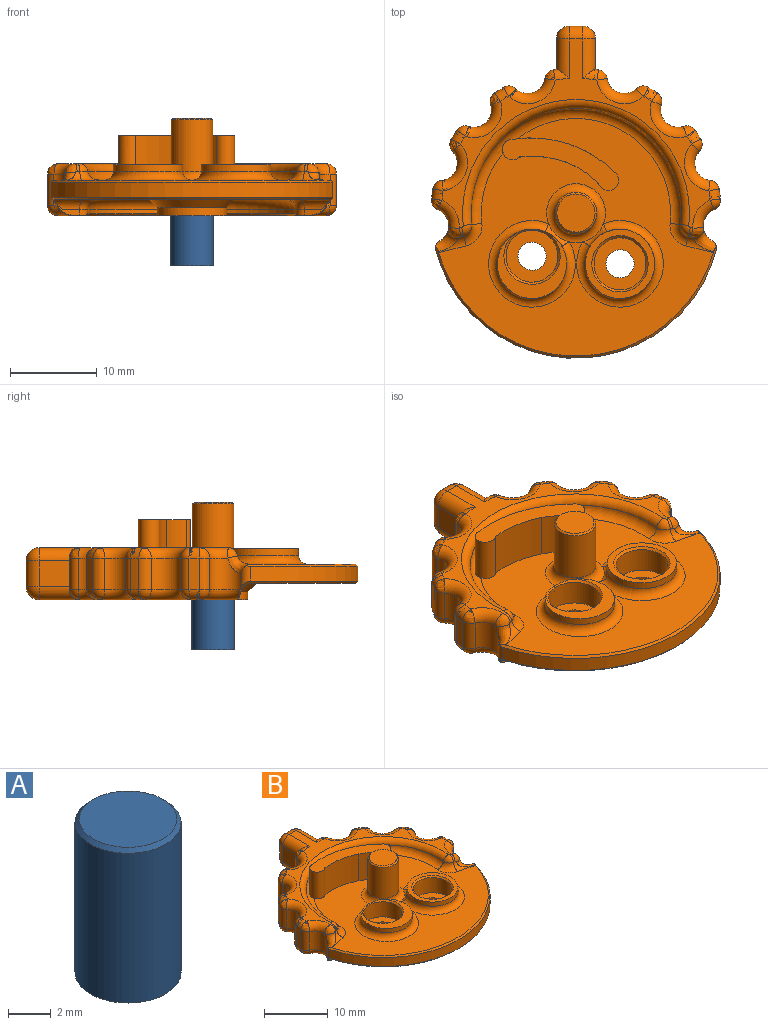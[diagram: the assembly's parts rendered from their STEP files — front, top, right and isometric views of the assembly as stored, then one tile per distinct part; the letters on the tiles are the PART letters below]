
ASSEMBLY  parts=2 mates=1
PART A: 4 faces, bbox 5x5x8.8 mm
  f0: cylinder r=2.48mm len=8.55mm, axis (0,0,-1), area 133mm2, adj f2,f3
  f1: plane 4.55x4.55mm, normal (0,0,1), area 16.3mm2, adj f3
  f2: plane 4.95x4.95mm, normal (0,0,-1), area 19.2mm2, adj f0
  f3: cone r=2.27mm half-angle=45deg, axis (0,0,-1), area 4.2mm2, adj f0,f1
PART B: 180 faces, bbox 33.4x38.4x11.5 mm
  f0: plane 31.71x27.42mm, normal (0,0,-1), area 478mm2, adj f1,f168,f169,f170,f171,f172,f173,f174
  f1: cylinder r=1.2mm len=3.47mm, axis (-0.97,0.24,0), area 5.1mm2, adj f0,f2,f168,f172
  f2: plane 2.59x1.21mm, normal (-0.24,-0.97,0), area 1.2mm2, adj f1,f3,f166,f167,f172
  f3: bspline ~1.85x1.33mm, area 0.3mm2, adj f2,f4,f165,f166
  f4: torus R=3.2mm, axis (0,0,1), area 8.5mm2, adj f3,f5,f163,f164
  f5: sphere r=1.2mm, area 1.8mm2, adj f4,f6,f162
  f6: cylinder r=1.2mm len=3.6mm, axis (0,0,1), area 5.5mm2, adj f5,f7,f161,f164
  f7: cylinder r=16.75mm len=3.6mm, axis (0,0,-1), area 4.3mm2, adj f6,f8,f160,f162
  f8: torus R=15.55mm, axis (0,0,1), area 2.2mm2, adj f7,f9,f159,f161
  f9: plane 30.96x21.83mm, normal (0,0,1), area 67mm2, adj f8,f10,f137,f138,f139,f140,f141,f142
  f10: cylinder r=1.5mm len=1.5mm, axis (1,0,0), area 3.5mm2, adj f9,f11,f135,f136
  f11: plane 3x1.5mm, normal (0,1,0), area 4.5mm2, adj f10,f12,f101,f134
  f12: cylinder r=1.5mm len=3mm, axis (0,0,1), area 7.1mm2, adj f11,f13,f100,f136
  f13: plane 3.5x3mm, normal (-1,0,0), area 10.5mm2, adj f12,f14,f99,f158
  f14: cylinder r=16.75mm len=3.6mm, axis (0,0,-1), area 1.3mm2, adj f13,f15,f98,f99,f157,f158
  f15: cylinder r=1.2mm len=3.6mm, axis (0,0,1), area 5.5mm2, adj f14,f16,f96,f97
  f16: cylinder r=2mm len=3.6mm, axis (0,0,-1), area 15.7mm2, adj f15,f17,f94,f156
  f17: torus R=3.2mm, axis (0,0,1), area 10mm2, adj f16,f18,f96,f163
  f18: sphere r=1.2mm, area 1mm2, adj f17,f19,f94
  f19: torus R=15.55mm, axis (0,0,1), area 2.2mm2, adj f18,f20,f93,f163
  f20: cylinder r=16.75mm len=3.6mm, axis (0,0,-1), area 4.3mm2, adj f19,f21,f94,f155
  f21: cylinder r=1.2mm len=3.6mm, axis (0,0,1), area 5.5mm2, adj f20,f22,f23,f93
  f22: sphere r=1.2mm, area 1mm2, adj f21,f154,f155
  f23: cylinder r=2mm len=3.6mm, axis (0,0,-1), area 15.8mm2, adj f21,f24,f91,f154
  f24: torus R=3.2mm, axis (0,0,1), area 10.1mm2, adj f23,f25,f93,f163
  f25: sphere r=1.2mm, area 1mm2, adj f24,f26,f91
  f26: torus R=15.55mm, axis (0,0,1), area 2.2mm2, adj f25,f27,f90,f163
  f27: cylinder r=16.75mm len=3.6mm, axis (0,0,-1), area 4.3mm2, adj f26,f28,f91,f153
  f28: cylinder r=1.2mm len=3.6mm, axis (0,0,1), area 5.6mm2, adj f27,f29,f30,f90
  f29: sphere r=1.2mm, area 1mm2, adj f28,f152,f153
  f30: cylinder r=2mm len=3.6mm, axis (0,0,-1), area 15.9mm2, adj f28,f31,f88,f152
  f31: torus R=3.2mm, axis (0,0,1), area 10.1mm2, adj f30,f32,f90,f163
  f32: sphere r=1.2mm, area 1mm2, adj f31,f33,f88
  f33: torus R=15.55mm, axis (0,0,1), area 2.2mm2, adj f32,f34,f87,f163
  f34: cylinder r=16.75mm len=3.6mm, axis (0,0,-1), area 4.3mm2, adj f33,f35,f88,f151
  f35: cylinder r=1.2mm len=3.6mm, axis (0,0,1), area 5.5mm2, adj f34,f36,f37,f87
  f36: sphere r=1.2mm, area 1mm2, adj f35,f150,f151
  f37: cylinder r=2mm len=3.6mm, axis (0,0,-1), area 13.7mm2, adj f35,f38,f47,f48,f86,f150,f172
  f38: torus R=3.2mm, axis (0,0,1), area 8.5mm2, adj f37,f39,f87,f163
  f39: bspline ~1.85x1.33mm, area 0.3mm2, adj f38,f40,f46,f47
  f40: plane 2.59x1.21mm, normal (0.24,-0.97,0), area 1.2mm2, adj f39,f41,f46,f171,f172
  f41: cylinder r=1.2mm len=1.3mm, axis (0,0,-1), area 1mm2, adj f40,f42,f43,f45,f170
  f42: cylinder r=12.12mm len=24.25mm, axis (0,0,-1), area 18.3mm2, adj f41,f43,f167,f169
  f43: cone r=12.37mm half-angle=45deg, axis (0,0,-1), area 14.9mm2, adj f41,f42,f44,f45,f163,f167
  f44: cone r=1.13mm half-angle=45deg, axis (0,0,1), area 0.1mm2, adj f43,f163,f166,f167
  f45: cone r=1.13mm half-angle=45deg, axis (0,0,1), area 0.1mm2, adj f41,f43,f46,f163
  f46: plane 0.79x0.26mm, normal (0.17,-0.69,-0.71), area 0.1mm2, adj f39,f40,f45,f163
  f47: plane 0.13x0.06mm, normal (-0.91,-0.41,0), area 0mm2, adj f37,f39,f172
  f48: cylinder r=1mm len=2.52mm, axis (0,0,1), area 2.5mm2, adj f37,f49,f85,f86,f172
  f49: cone r=16.5mm half-angle=45deg, axis (0,0,-1), area 15.6mm2, adj f48,f50,f79,f81,f82,f83,f85,f86
  f50: plane 31.71x27.42mm, normal (0,0,1), area 353.1mm2, adj f49,f51,f53,f54,f55,f56,f57,f58
  f51: cylinder r=1.18mm len=5.15mm, axis (0,0,-1), area 24.1mm2, adj f50,f52,f53,f57,f58
  f52: plane 13.41x6.07mm, normal (0,0,1), area 30.4mm2, adj f51,f53,f54,f56,f57
  f53: cylinder r=11.53mm len=6.5mm, axis (0,0,-1), area 34.4mm2, adj f50,f51,f52,f54
  f54: cylinder r=9.21mm len=7.81mm, axis (0,0,-1), area 19.3mm2, adj f50,f52,f53,f55,f56,f175
  f55: cylinder r=1.18mm len=2.66mm, axis (0,0,-1), area 0.1mm2, adj f50,f54,f175
  f56: cylinder r=1.18mm len=5.15mm, axis (0,0,-1), area 19.7mm2, adj f50,f52,f54,f57
  f57: cylinder r=13.74mm len=11.77mm, axis (0,0,-1), area 66.2mm2, adj f50,f51,f52,f56,f58
  f58: torus R=10.92mm, axis (0,0,1), area 66.3mm2, adj f50,f51,f57,f59,f60,f147
  f59: torus R=2.4mm, axis (0,0,1), area 4.2mm2, adj f50,f58,f79,f146
  f60: torus R=2.4mm, axis (0,0,1), area 4.2mm2, adj f50,f58,f83,f148
  f61: torus R=5mm, axis (0,0,1), area 38.6mm2, adj f50,f62,f63
  f62: bspline ~2.78x2.59mm, area 3mm2, adj f61,f63,f75
  f63: cylinder r=4mm len=8mm, axis (0,0,-1), area 20.1mm2, adj f61,f62,f64
  f64: plane 8x8mm, normal (0,0,1), area 17.1mm2, adj f63,f65
  f65: cone r=3.25mm half-angle=45deg, axis (0,0,1), area 6.9mm2, adj f64,f66
  f66: cylinder r=3mm len=6mm, axis (0,0,-1), area 54.7mm2, adj f65,f67
  f67: plane 6x6mm, normal (0,0,1), area 20mm2, adj f66,f173
  f68: torus R=5mm, axis (0,0,1), area 38.6mm2, adj f50,f69,f70
  f69: bspline ~2.78x2.59mm, area 3mm2, adj f68,f70,f75
  f70: cylinder r=4mm len=8mm, axis (0,0,-1), area 20.1mm2, adj f68,f69,f71,f72
  f71: plane 8x7.53mm, normal (0,0,1), area 17.4mm2, adj f70,f72
  f72: cone r=3.25mm half-angle=45deg, axis (0,0,1), area 6.4mm2, adj f70,f71,f73
  f73: cylinder r=3mm len=6mm, axis (0,0,-1), area 54.7mm2, adj f72,f74
  f74: plane 6x6mm, normal (0,0,1), area 20mm2, adj f73,f174
  f75: torus R=3.4mm, axis (0,0,1), area 27.3mm2, adj f50,f62,f69,f76
  f76: cylinder r=2.4mm len=5.95mm, axis (0,0,-1), area 89.7mm2, adj f75,f77
  f77: cone r=2.2mm half-angle=45deg, axis (0,0,-1), area 4.1mm2, adj f76,f78
  f78: plane 4.4x4.4mm, normal (0,0,1), area 15.2mm2, adj f77
  f79: cylinder r=1.2mm len=3.47mm, axis (0.97,-0.24,0), area 2.1mm2, adj f49,f50,f59,f80,f81,f145
  f80: bspline ~1.68x1.45mm, area 2.2mm2, adj f79,f81,f144,f145
  f81: bspline ~2.96x2.87mm, area 5.1mm2, adj f49,f79,f80,f82,f164
  f82: cylinder r=1mm len=2.52mm, axis (0,0,1), area 2.5mm2, adj f49,f81,f85,f164,f172
  f83: cylinder r=1.2mm len=3.47mm, axis (0.97,0.24,0), area 2.1mm2, adj f49,f50,f60,f84,f86,f149
  f84: bspline ~1.76x1.44mm, area 2.2mm2, adj f83,f86,f149,f150
  f85: cylinder r=16.75mm len=32.36mm, axis (0,0,-1), area 74.5mm2, adj f48,f49,f82,f172
  f86: bspline ~2.96x2.87mm, area 5.1mm2, adj f37,f48,f49,f83,f84
  f87: sphere r=1.2mm, area 2.7mm2, adj f33,f35,f38
  f88: cylinder r=1.2mm len=3.6mm, axis (0,0,1), area 5.6mm2, adj f30,f32,f34,f89
  f89: sphere r=1.2mm, area 2.7mm2, adj f88,f151,f152
  f90: sphere r=1.2mm, area 2.7mm2, adj f26,f28,f31
  f91: cylinder r=1.2mm len=3.6mm, axis (0,0,1), area 5.5mm2, adj f23,f25,f27,f92
  f92: sphere r=1.2mm, area 3.3mm2, adj f91,f153,f154
  f93: sphere r=1.2mm, area 2.7mm2, adj f19,f21,f24
  f94: cylinder r=1.2mm len=3.6mm, axis (0,0,1), area 5.5mm2, adj f16,f18,f20,f95
  f95: sphere r=1.2mm, area 3.1mm2, adj f94,f155,f156
  f96: sphere r=1.2mm, area 2.7mm2, adj f15,f17,f98
  f97: sphere r=1.2mm, area 1mm2, adj f15,f156,f157
  f98: torus R=15.55mm, axis (0,0,1), area 2mm2, adj f14,f96,f99,f163
  f99: cylinder r=1.5mm len=4.57mm, axis (0,-1,0), area 9mm2, adj f13,f14,f98,f100,f163
  f100: sphere r=1.5mm, area 4.8mm2, adj f12,f99,f101
  f101: cylinder r=1.5mm len=1.5mm, axis (-1,0,0), area 3.5mm2, adj f11,f100,f102,f163
  f102: sphere r=1.5mm, area 2.3mm2, adj f101,f103,f134
  f103: cylinder r=1.5mm len=4.57mm, axis (0,1,0), area 9mm2, adj f102,f104,f132,f133,f163
  f104: cylinder r=16.75mm len=3.6mm, axis (0,0,-1), area 1.3mm2, adj f103,f105,f132,f133,f137,f138
  f105: cylinder r=1.2mm len=3.6mm, axis (0,0,1), area 5.5mm2, adj f104,f106,f130,f131
  f106: cylinder r=2mm len=3.6mm, axis (0,0,-1), area 15.7mm2, adj f105,f107,f128,f139
  f107: cylinder r=1.2mm len=3.6mm, axis (0,0,1), area 5.5mm2, adj f106,f108,f126,f127
  f108: cylinder r=16.75mm len=3.6mm, axis (0,0,-1), area 4.3mm2, adj f107,f109,f124,f140
  f109: torus R=15.55mm, axis (0,0,1), area 2.2mm2, adj f108,f110,f127,f163
  f110: sphere r=1.2mm, area 1.3mm2, adj f109,f111,f124
  f111: torus R=3.2mm, axis (0,0,1), area 10.1mm2, adj f110,f112,f123,f163
  f112: sphere r=1.2mm, area 1.8mm2, adj f111,f113,f121
  f113: torus R=15.55mm, axis (0,0,1), area 2.2mm2, adj f112,f114,f120,f163
  f114: sphere r=1.2mm, area 1.6mm2, adj f113,f115,f118
  f115: torus R=3.2mm, axis (0,0,1), area 10.1mm2, adj f114,f116,f117,f163
  f116: sphere r=1.2mm, area 1.9mm2, adj f115,f160,f162
  f117: cylinder r=2mm len=3.6mm, axis (0,0,-1), area 15.9mm2, adj f115,f118,f143,f160
  f118: cylinder r=1.2mm len=3.6mm, axis (0,0,1), area 5.6mm2, adj f114,f117,f119,f120
  f119: sphere r=1.2mm, area 2.7mm2, adj f118,f142,f143
  f120: cylinder r=16.75mm len=3.6mm, axis (0,0,-1), area 4.3mm2, adj f113,f118,f121,f142
  f121: cylinder r=1.2mm len=3.6mm, axis (0,0,1), area 5.5mm2, adj f112,f120,f122,f123
  f122: sphere r=1.2mm, area 1.3mm2, adj f121,f141,f142
  f123: cylinder r=2mm len=3.6mm, axis (0,0,-1), area 15.8mm2, adj f111,f121,f124,f141
  f124: cylinder r=1.2mm len=3.6mm, axis (0,0,1), area 5.5mm2, adj f108,f110,f123,f125
  f125: sphere r=1.2mm, area 2.7mm2, adj f124,f140,f141
  f126: sphere r=1.2mm, area 1.6mm2, adj f107,f139,f140
  f127: sphere r=1.2mm, area 1.8mm2, adj f107,f109,f128
  f128: torus R=3.2mm, axis (0,0,1), area 10mm2, adj f106,f127,f129,f131,f163
  f129: sphere r=1.2mm, area 0.3mm2, adj f128,f133
  f130: sphere r=1.2mm, area 2.7mm2, adj f105,f138,f139
  f131: sphere r=1.2mm, area 0.6mm2, adj f105,f128,f133
  f132: plane 3.5x3mm, normal (1,0,0), area 10.5mm2, adj f103,f104,f134,f137
  f133: torus R=15.55mm, axis (0,0,1), area 2mm2, adj f103,f104,f129,f131,f163
  f134: cylinder r=1.5mm len=3mm, axis (0,0,-1), area 7.1mm2, adj f11,f102,f132,f135
  f135: sphere r=1.5mm, area 2.3mm2, adj f10,f134,f137
  f136: sphere r=1.5mm, area 4.8mm2, adj f10,f12,f158
  f137: cylinder r=1.5mm len=4.57mm, axis (0,-1,0), area 9mm2, adj f9,f104,f132,f135,f138
  f138: torus R=15.55mm, axis (0,0,1), area 2mm2, adj f9,f104,f130,f137
  f139: torus R=3.2mm, axis (0,0,1), area 10mm2, adj f9,f106,f126,f130
  f140: torus R=15.55mm, axis (0,0,1), area 2.2mm2, adj f9,f108,f125,f126
  f141: torus R=3.2mm, axis (0,0,1), area 10.1mm2, adj f9,f122,f123,f125
  f142: torus R=15.55mm, axis (0,0,1), area 2.2mm2, adj f9,f119,f120,f122
  f143: torus R=3.2mm, axis (0,0,1), area 10.1mm2, adj f9,f117,f119,f159
  f144: torus R=3.2mm, axis (0,0,1), area 5.9mm2, adj f9,f80,f161,f164
  f145: cylinder r=1mm len=1.04mm, axis (0.97,-0.24,0), area 0.4mm2, adj f9,f79,f80,f146
  f146: torus R=0.22mm, axis (0,0,-1), area 1.7mm2, adj f9,f59,f145,f147
  f147: torus R=13.1mm, axis (0,0,1), area 60.2mm2, adj f9,f58,f146,f148
  f148: torus R=0.22mm, axis (0,0,-1), area 1.7mm2, adj f9,f60,f147,f149
  f149: cylinder r=1mm len=1.04mm, axis (0.97,0.24,0), area 0.4mm2, adj f9,f83,f84,f148
  f150: torus R=3.2mm, axis (0,0,1), area 5.9mm2, adj f9,f36,f37,f84
  f151: torus R=15.55mm, axis (0,0,1), area 2.2mm2, adj f9,f34,f36,f89
  f152: torus R=3.2mm, axis (0,0,1), area 10.1mm2, adj f9,f29,f30,f89
  f153: torus R=15.55mm, axis (0,0,1), area 2.2mm2, adj f9,f27,f29,f92
  f154: torus R=3.2mm, axis (0,0,1), area 10.1mm2, adj f9,f22,f23,f92
  f155: torus R=15.55mm, axis (0,0,1), area 2.2mm2, adj f9,f20,f22,f95
  f156: torus R=3.2mm, axis (0,0,1), area 10mm2, adj f9,f16,f95,f97
  f157: torus R=15.55mm, axis (0,0,1), area 2mm2, adj f9,f14,f97,f158
  f158: cylinder r=1.5mm len=4.57mm, axis (0,1,0), area 9mm2, adj f9,f13,f14,f136,f157
  f159: sphere r=1.2mm, area 1.9mm2, adj f8,f143,f160
  f160: cylinder r=1.2mm len=3.6mm, axis (0,0,1), area 5.6mm2, adj f7,f116,f117,f159
  f161: sphere r=1.2mm, area 2.7mm2, adj f6,f8,f144
  f162: torus R=15.55mm, axis (0,0,1), area 2.2mm2, adj f5,f7,f116,f163
  f163: plane 30.96x22.83mm, normal (0,0,-1), area 100.8mm2, adj f4,f17,f19,f24,f26,f31,f33,f38
  f164: cylinder r=2mm len=3.6mm, axis (0,0,-1), area 13.7mm2, adj f4,f6,f81,f82,f144,f165,f172
  f165: plane 0.13x0.06mm, normal (0.91,-0.41,0), area 0mm2, adj f3,f164,f172
  f166: plane 0.79x0.26mm, normal (-0.17,-0.69,-0.71), area 0.1mm2, adj f2,f3,f44,f163
  f167: cylinder r=1.2mm len=1.3mm, axis (0,0,-1), area 1mm2, adj f2,f42,f43,f44,f168
  f168: torus R=2.4mm, axis (0,0,1), area 4.4mm2, adj f0,f1,f167,f169
  f169: torus R=10.92mm, axis (0,0,1), area 74mm2, adj f0,f42,f168,f170
  f170: torus R=2.4mm, axis (0,0,1), area 4.4mm2, adj f0,f41,f169,f171
  f171: cylinder r=1.2mm len=3.47mm, axis (-0.97,-0.24,0), area 5.1mm2, adj f0,f40,f170,f172
  f172: cone r=16.75mm half-angle=45deg, axis (0,0,1), area 16.6mm2, adj f0,f1,f2,f37,f40,f47,f48,f82
  f173: cylinder r=1.62mm len=3.25mm, axis (0,0,-1), area 8.7mm2, adj f0,f67
  f174: cylinder r=1.62mm len=3.25mm, axis (0,0,-1), area 8.7mm2, adj f0,f74
  f175: torus R=5mm, axis (0,0,1), area 43.1mm2, adj f0,f54,f55,f176
  f176: cylinder r=4mm len=8mm, axis (0,0,1), area 22.6mm2, adj f175,f177
  f177: plane 8x8mm, normal (0,0,-1), area 32.2mm2, adj f176,f178
  f178: cylinder r=2.4mm len=4.8mm, axis (0,0,-1), area 45.2mm2, adj f177,f179
  f179: plane 4.8x4.8mm, normal (0,0,-1), area 18.1mm2, adj f178
PLACE A t=(7.39,-7.94,-8.17)mm
PLACE B t=(7.39,-7.94,0.61)mm
MATE slider A.f0 <-> B.f75  axis (0,0,-1) through (7.39,-7.94,-8.17)mm
